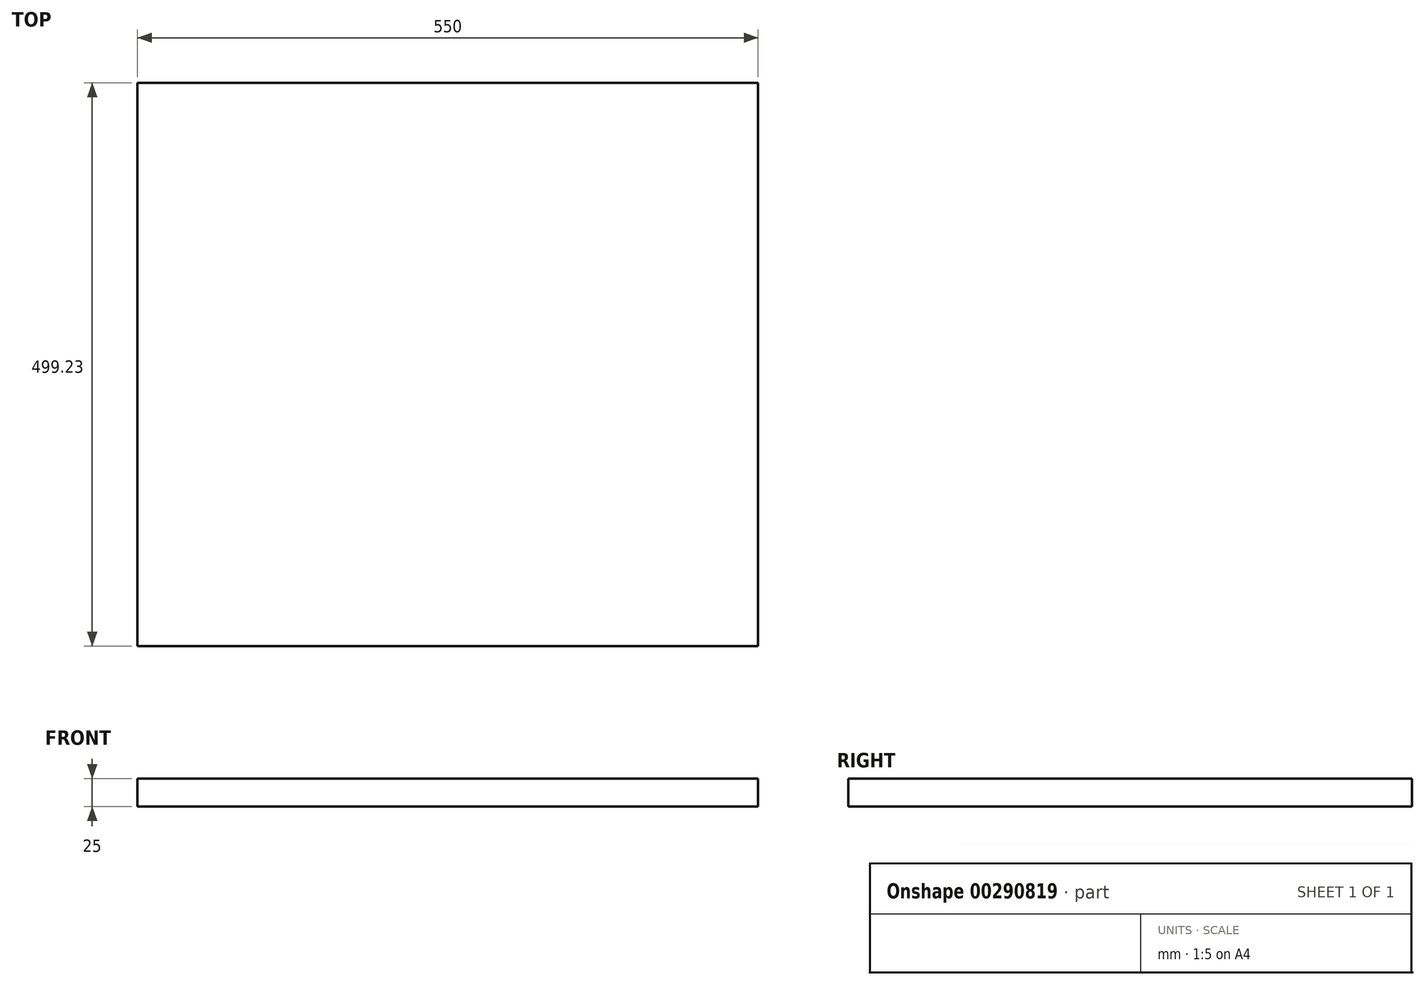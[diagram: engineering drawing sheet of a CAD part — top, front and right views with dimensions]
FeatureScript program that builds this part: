
annotation { "Feature Type Name" : "Feature", "Feature Type Description" : "" }
export const myFeature = defineFeature(function(context is Context, id is Id, definition is map)
    precondition{}
    {
        {
            var Q0;
            Q0=qCreatedBy(makeId("Top.planeOp"),FACE);
            var sketch = newSketch(context, id + "F0", { "sketchPlane" : qUnion([Q0])});
            skLineSegment(sketch, "E0.bottom", {"start": v(274.73, -249.35) * mm, "end": v(-275.27, -249.35) * mm});
            skLineSegment(sketch, "E0.top", {"start": v(274.73, 249.88) * mm, "end": v(-275.27, 249.88) * mm});
            skLineSegment(sketch, "E0.left", {"start": v(274.73, -249.35) * mm, "end": v(274.73, 249.88) * mm});
            skLineSegment(sketch, "E0.right", {"start": v(-275.27, -249.35) * mm, "end": v(-275.27, 249.88) * mm});
            skPoint(sketch, "E0.middle", {"position": v(-0.27, 0.27) * mm});
            skSolve(sketch);
        }
        {
            var Q0;
            Q0=makeQuery(id+"F0.imprint","IMPRINT",FACE,{"disambiguationData":[TD([[makeQuery(id+"F0.imprint","IMPRINT",EDGE,{"derivedFrom":sQuery(id+"F0.wireOp",EDGE,"E0.bottom")}),-1.0]])]});
            extrude(context, id + "F1", {"entities" : qUnion([Q0]), "depth" : 50 * mm});
        }
        {
            var Q0;
            Q0=makeQuery(id+"F1.opExtrude","CAP_FACE",FACE,{"disambiguationData":[OSD([sQuery(id+"F0.wireOp",EDGE,"E0.bottom"),sQuery(id+"F0.wireOp",EDGE,"E0.top"),sQuery(id+"F0.wireOp",EDGE,"E0.left"),sQuery(id+"F0.wireOp",EDGE,"E0.right")])],"isStart":false});
            var sketch = newSketch(context, id + "F2", { "sketchPlane" : qUnion([Q0])});
            skSolve(sketch);
        }
        {
            var Q0;
            Q0 = qSketchRegion(id + "F2", true);
            var Q1;
            Q1=makeQuery(id+"F2.imprint","IMPRINT",FACE,{"disambiguationData":[TD([[makeQuery(id+"F2.imprint","IMPRINT",EDGE,{"derivedFrom":makeQuery(id+"F1.opExtrude","CAP_EDGE",EDGE,{"disambiguationData":[OSD([sQuery(id+"F0.wireOp",EDGE,"E0.bottom")])],"isStart":false})}),-1.0]])]});
            extrude(context, id + "F3", {"entities" : qUnion([Q0, Q1]), "operationType" : NewBodyOperationType.REMOVE, "oppositeDirection" : true, "depth" : 25 * mm});
        }
    });
